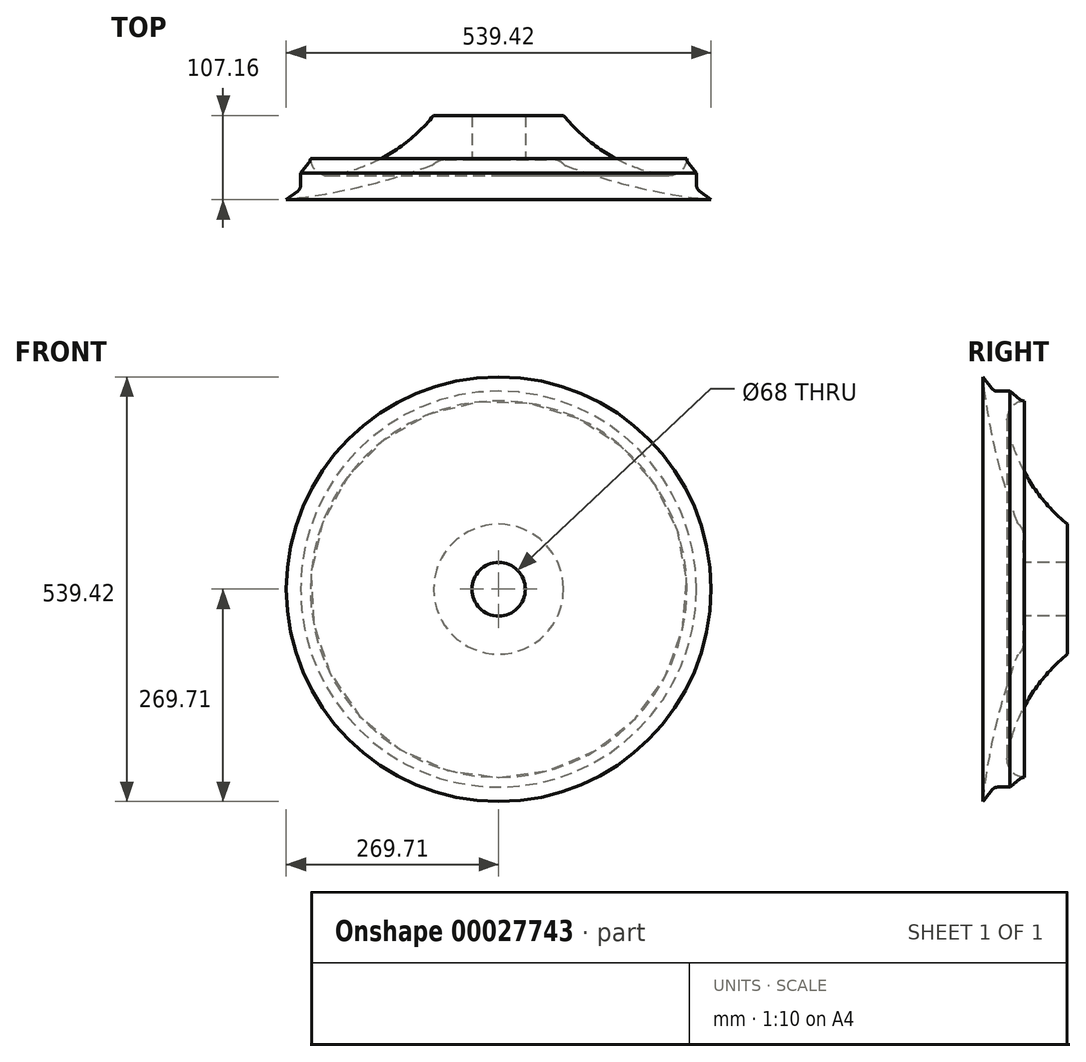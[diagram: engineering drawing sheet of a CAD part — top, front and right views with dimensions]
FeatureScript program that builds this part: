
annotation { "Feature Type Name" : "Feature", "Feature Type Description" : "" }
export const myFeature = defineFeature(function(context is Context, id is Id, definition is map)
    precondition{}
    {
        {
            var Q0;
            Q0=qCreatedBy(makeId("Right.planeOp"),FACE);
            var sketch = newSketch(context, id + "F0", { "sketchPlane" : qUnion([Q0])});
            skLineSegment(sketch, "E0", {"start": v(-123.86, 254) * mm, "end": v(-109.52, 254) * mm, "construction": true});
            skLineSegment(sketch, "E1", {"start": v(0, 0) * mm, "end": v(0, 254) * mm, "construction": true});
            skPoint(sketch, "E1.endSnap0", {"position": v(0, 254) * mm});
            skLineSegment(sketch, "E2", {"start": v(-140.14, 271.25) * mm, "end": v(-128.9, 256.5) * mm});
            skLineSegment(sketch, "E3", {"start": v(-105.46, 252.53) * mm, "end": v(-94.14, 243.13) * mm});
            skLineSegment(sketch, "E4", {"start": v(-89.81, 241.67) * mm, "end": v(77.91, 248.76) * mm});
            skLineSegment(sketch, "E5", {"start": v(79.7, 249.1) * mm, "end": v(93.05, 253.66) * mm});
            skLineSegment(sketch, "E6", {"start": v(95.1, 254) * mm, "end": v(123.47, 254) * mm});
            skLineSegment(sketch, "E7", {"start": v(128.86, 257) * mm, "end": v(138.45, 272.41) * mm});
            skPoint(sketch, "E8.visualSharp", {"position": v(-127, 254) * mm});
            skArc(sketch, "E8.filletArc", {"start": v(-128.9, 256.5) * mm, "mid": v(-126.67, 254.66) * mm, "end": v(-123.86, 254) * mm});
            skPoint(sketch, "E9.newPointA", {"position": v(127, 254) * mm});
            skArc(sketch, "E9.filletArc", {"start": v(-105.46, 252.53) * mm, "mid": v(-107.36, 253.62) * mm, "end": v(-109.52, 254) * mm});
            skPoint(sketch, "E10.visualSharp", {"position": v(-92.26, 241.57) * mm});
            skArc(sketch, "E10.filletArc", {"start": v(-94.14, 243.13) * mm, "mid": v(-92.11, 242) * mm, "end": v(-89.81, 241.67) * mm});
            skPoint(sketch, "E11.visualSharp", {"position": v(78.83, 248.8) * mm});
            skArc(sketch, "E11.filletArc", {"start": v(77.91, 248.76) * mm, "mid": v(78.82, 248.86) * mm, "end": v(79.7, 249.1) * mm});
            skPoint(sketch, "E12.visualSharp", {"position": v(94.04, 254) * mm});
            skArc(sketch, "E12.filletArc", {"start": v(95.1, 254) * mm, "mid": v(94.06, 253.91) * mm, "end": v(93.05, 253.66) * mm});
            skArc(sketch, "E13.filletArc", {"start": v(123.47, 254) * mm, "mid": v(126.56, 254.8) * mm, "end": v(128.86, 257) * mm});
            skSolve(sketch);
        }
        {
            var Q0;
            Q0=qCreatedBy(makeId("Right.planeOp"),FACE);
            var sketch = newSketch(context, id + "F1", { "sketchPlane" : qUnion([Q0])});
            skLineSegment(sketch, "E14.0", {"start": v(131.02, 255.65) * mm, "end": v(140.61, 271.07) * mm});
            skLineSegment(sketch, "E14.1", {"start": v(-108.14, 251.46) * mm, "end": v(-95.76, 241.18) * mm});
            skLineSegment(sketch, "E14.2", {"start": v(-123.86, 251.46) * mm, "end": v(-108.14, 251.46) * mm});
            skArc(sketch, "E14.3", {"start": v(-130.93, 254.96) * mm, "mid": v(-127.8, 252.38) * mm, "end": v(-123.86, 251.46) * mm});
            skLineSegment(sketch, "E14.4", {"start": v(-142.16, 269.7) * mm, "end": v(-130.93, 254.96) * mm});
            skArc(sketch, "E14.5", {"start": v(-95.76, 241.18) * mm, "mid": v(-92.93, 239.6) * mm, "end": v(-89.7, 239.13) * mm});
            skLineSegment(sketch, "E14.6", {"start": v(-89.7, 239.13) * mm, "end": v(78.02, 246.22) * mm});
            skArc(sketch, "E14.7", {"start": v(78.02, 246.22) * mm, "mid": v(79.29, 246.37) * mm, "end": v(80.52, 246.7) * mm});
            skLineSegment(sketch, "E14.8", {"start": v(80.52, 246.7) * mm, "end": v(94.47, 251.46) * mm});
            skLineSegment(sketch, "E14.9", {"start": v(94.47, 251.46) * mm, "end": v(123.47, 251.46) * mm});
            skArc(sketch, "E14.10", {"start": v(123.47, 251.46) * mm, "mid": v(127.79, 252.58) * mm, "end": v(131.02, 255.65) * mm});
            skLineSegment(sketch, "E15.0", {"start": v(-105.46, 252.53) * mm, "end": v(-94.14, 243.13) * mm});
            skLineSegment(sketch, "E15.1", {"start": v(-140.14, 271.25) * mm, "end": v(-128.9, 256.5) * mm});
            skArc(sketch, "E15.2", {"start": v(-128.9, 256.5) * mm, "mid": v(-126.67, 254.66) * mm, "end": v(-123.86, 254) * mm});
            skLineSegment(sketch, "E15.3", {"start": v(-123.86, 254) * mm, "end": v(-109.52, 254) * mm});
            skArc(sketch, "E15.4", {"start": v(-105.46, 252.53) * mm, "mid": v(-107.36, 253.62) * mm, "end": v(-109.52, 254) * mm});
            skPoint(sketch, "E15.5", {"position": v(-92.26, 241.57) * mm});
            skArc(sketch, "E15.6", {"start": v(-94.14, 243.13) * mm, "mid": v(-92.11, 242) * mm, "end": v(-89.81, 241.67) * mm});
            skLineSegment(sketch, "E15.7", {"start": v(-89.81, 241.67) * mm, "end": v(77.91, 248.76) * mm});
            skLineSegment(sketch, "E15.8", {"start": v(128.86, 257) * mm, "end": v(138.45, 272.41) * mm});
            skArc(sketch, "E15.9", {"start": v(123.47, 254) * mm, "mid": v(126.56, 254.8) * mm, "end": v(128.86, 257) * mm});
            skLineSegment(sketch, "E15.10", {"start": v(95.1, 254) * mm, "end": v(123.47, 254) * mm});
            skArc(sketch, "E15.11", {"start": v(95.1, 254) * mm, "mid": v(94.06, 253.91) * mm, "end": v(93.05, 253.66) * mm});
            skLineSegment(sketch, "E15.12", {"start": v(79.7, 249.1) * mm, "end": v(93.05, 253.66) * mm});
            skArc(sketch, "E15.13", {"start": v(77.91, 248.76) * mm, "mid": v(78.82, 248.86) * mm, "end": v(79.7, 249.1) * mm});
            skLineSegment(sketch, "E16", {"start": v(-140.14, 271.25) * mm, "end": v(-142.16, 269.7) * mm});
            skLineSegment(sketch, "E17", {"start": v(138.45, 272.41) * mm, "end": v(140.61, 271.07) * mm});
            skLineSegment(sketch, "E18", {"start": v(0, 0) * mm, "end": v(-132.17, 0) * mm, "construction": true});
            skSolve(sketch);
        }
        {
            var Q0;
            Q0=qCreatedBy(makeId("Right.planeOp"),FACE);
            var sketch = newSketch(context, id + "F2", { "sketchPlane" : qUnion([Q0])});
            skLineSegment(sketch, "E19", {"start": v(-35, 0) * mm, "end": v(-35, 116.08) * mm, "construction": true});
            skLineSegment(sketch, "E20", {"start": v(0, 34) * mm, "end": v(-35, 34) * mm, "construction": true});
            skLineSegment(sketch, "E21", {"start": v(0, 57.15) * mm, "end": v(-35, 57.15) * mm, "construction": true});
            skLineSegment(sketch, "E22", {"start": v(-35, 34) * mm, "end": v(-90.96, 34) * mm});
            skLineSegment(sketch, "E23", {"start": v(-35, 34) * mm, "end": v(-35, 82.55) * mm});
            skArc(sketch, "E24", {"start": v(-111.34, 212.33) * mm, "mid": v(-85.02, 140.47) * mm, "end": v(-35, 82.55) * mm});
            skArc(sketch, "E25", {"start": v(-89.7, 239.13) * mm, "mid": v(-106.58, 230.62) * mm, "end": v(-111.34, 212.33) * mm});
            skArc(sketch, "E26.0", {"start": v(-95.76, 241.18) * mm, "mid": v(-92.93, 239.6) * mm, "end": v(-89.7, 239.13) * mm});
            skLineSegment(sketch, "E26.1", {"start": v(-123.86, 251.46) * mm, "end": v(-108.14, 251.46) * mm});
            skLineSegment(sketch, "E26.2", {"start": v(-108.14, 251.46) * mm, "end": v(-95.76, 241.18) * mm});
            skArc(sketch, "E26.3", {"start": v(-130.93, 254.96) * mm, "mid": v(-127.8, 252.38) * mm, "end": v(-123.86, 251.46) * mm});
            skLineSegment(sketch, "E26.4", {"start": v(-142.16, 269.7) * mm, "end": v(-130.93, 254.96) * mm});
            skLineSegment(sketch, "E27", {"start": v(-90.96, 34) * mm, "end": v(-90.96, 68.2) * mm});
            skArc(sketch, "E28", {"start": v(-90.96, 68.2) * mm, "mid": v(-92.63, 76.26) * mm, "end": v(-97.37, 83) * mm});
            skArc(sketch, "E29", {"start": v(-142.16, 269.7) * mm, "mid": v(-126.3, 176.22) * mm, "end": v(-98.98, 85.42) * mm});
            skPoint(sketch, "E30.visualSharp", {"position": v(-98.42, 83.91) * mm});
            skArc(sketch, "E30.filletArc", {"start": v(-98.98, 85.42) * mm, "mid": v(-98.32, 84.11) * mm, "end": v(-97.37, 83) * mm});
            skLineSegment(sketch, "E31", {"start": v(-132.89, 0) * mm, "end": v(0, 0) * mm, "construction": true});
            skSolve(sketch);
        }
        {
            var Q0;
            Q0 = qSketchRegion(id + "F2", true);
            var Q1;
            Q1=sQuery(id+"F2.wireOp",EDGE,"E31");
            revolve(context, id + "F3", {"entities" : qUnion([Q0]), "axis" : qUnion([Q1]), "revolveType" : RevolveType.FULL});
        }
    });
